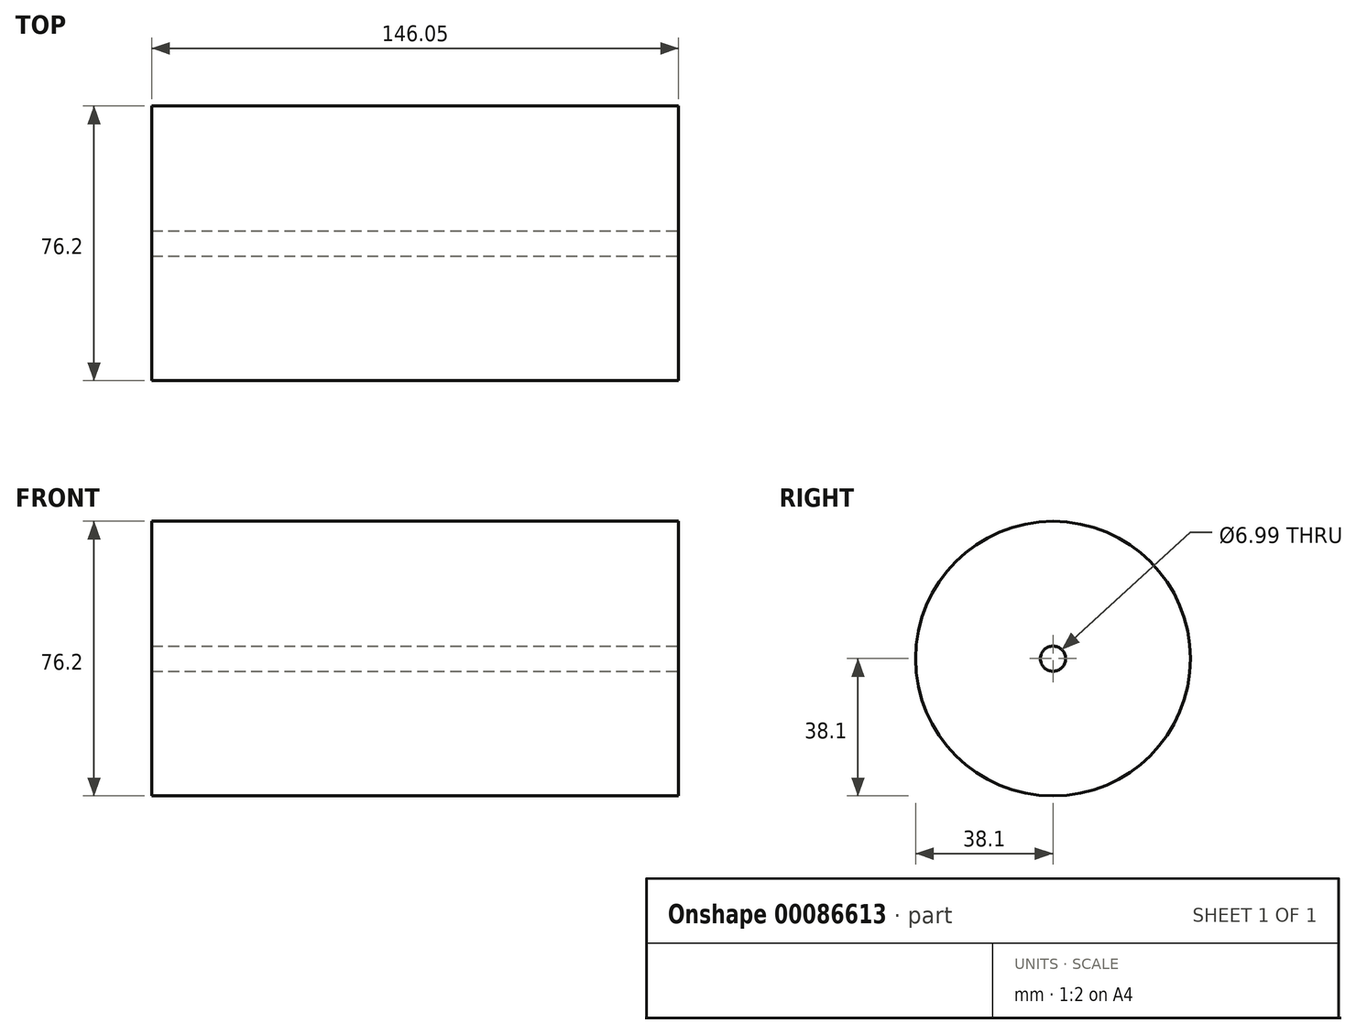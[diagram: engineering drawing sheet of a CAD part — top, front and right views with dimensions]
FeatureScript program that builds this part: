
annotation { "Feature Type Name" : "Feature", "Feature Type Description" : "" }
export const myFeature = defineFeature(function(context is Context, id is Id, definition is map)
    precondition{}
    {
        {
            var Q0;
            Q0=qCreatedBy(makeId("Right.planeOp"),FACE);
            var sketch = newSketch(context, id + "F0", { "sketchPlane" : qUnion([Q0])});
            skCircle(sketch, "E0", {"center": v(0, 0) * mm, "radius": 38.1 * mm});
            skSolve(sketch);
        }
        {
            var Q0;
            Q0 = qSketchRegion(id + "F0", true);
            extrude(context, id + "F1", {"entities" : qUnion([Q0]), "depth" : 146.05 * mm});
        }
        {
            var Q0;
            Q0=makeQuery(id+"F1.opExtrude","CAP_FACE",FACE,{"disambiguationData":[OSD([sQuery(id+"F0.wireOp",EDGE,"E0")])],"isStart":false});
            var sketch = newSketch(context, id + "F2", { "sketchPlane" : qUnion([Q0])});
            skCircle(sketch, "E1", {"center": v(0, 0) * mm, "radius": 3.5 * mm});
            skSolve(sketch);
        }
        {
            var Q0;
            Q0=sQuery(id+"F2.wireOp",VERTEX,"E1.center");
            var Q1;
            Q1=makeQuery(id+"F1.opExtrude","SWEPT_BODY",BODY,{"disambiguationData":[OSD([sQuery(id+"F0.wireOp",EDGE,"E0")])]});
            hole(context, id + "F3", {"style" : HoleStyle.SIMPLE, "endStyle" : HoleEndStyle.THROUGH, "holeDiameter" : 7 * mm, "locations" : qUnion([Q0]), "scope" : qUnion([Q1]), "isTappedThrough" : true});
        }
    });
